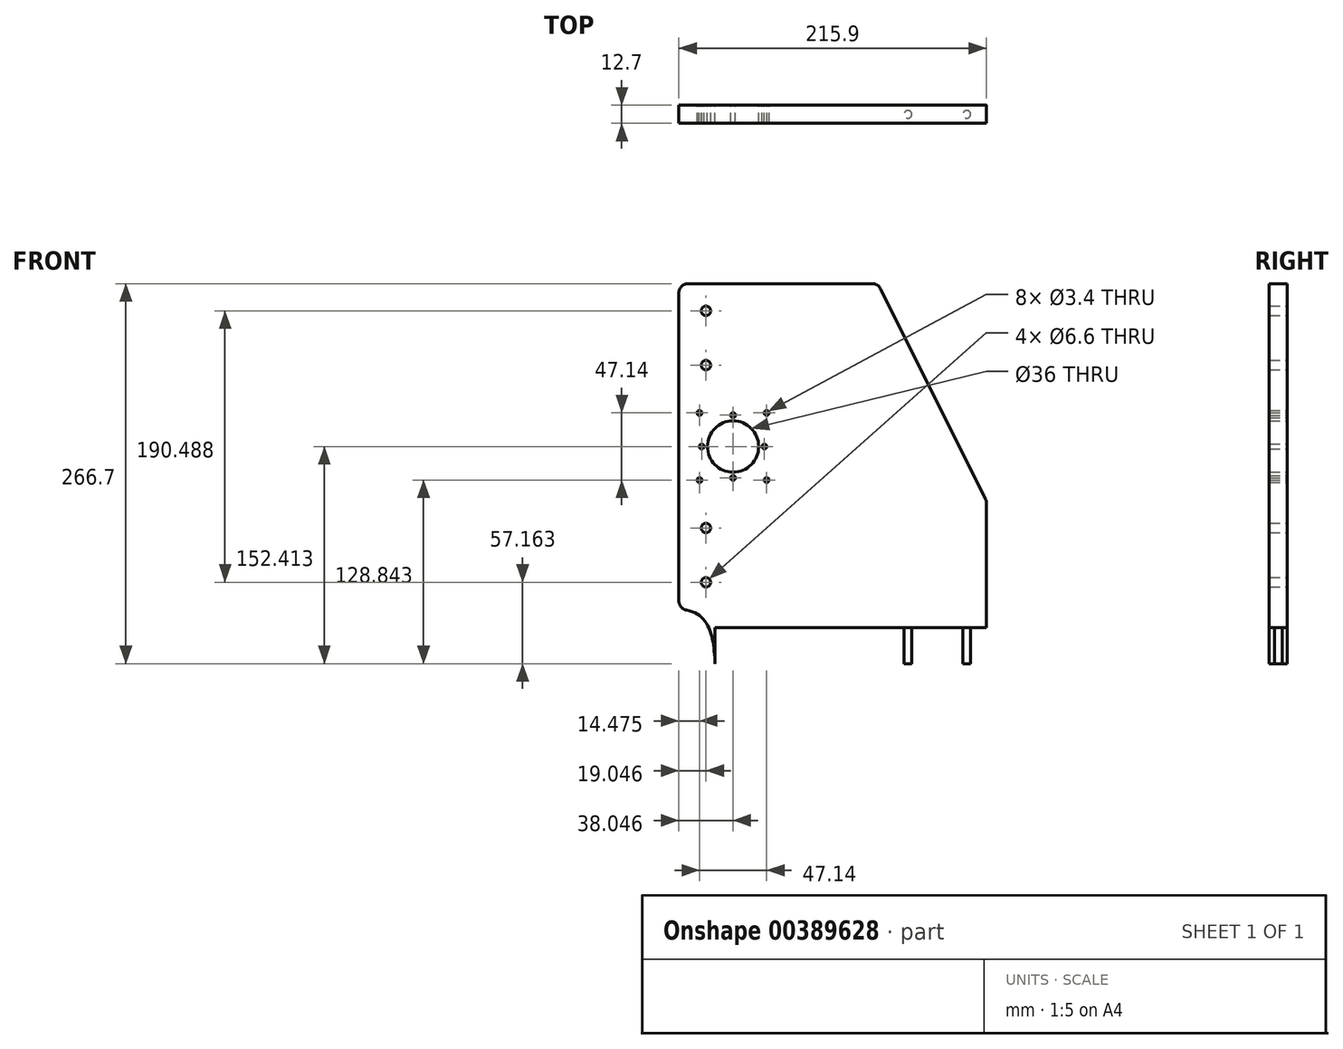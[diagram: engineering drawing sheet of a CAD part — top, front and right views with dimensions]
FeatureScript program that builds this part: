
annotation { "Feature Type Name" : "Feature", "Feature Type Description" : "" }
export const myFeature = defineFeature(function(context is Context, id is Id, definition is map)
    precondition{}
    {
        {
            var Q0;
            Q0=qCreatedBy(makeId("Front.planeOp"),FACE);
            var sketch = newSketch(context, id + "F0", { "sketchPlane" : qUnion([Q0])});
            skLineSegment(sketch, "E0.bottom", {"start": v(108.43, 152.4) * mm, "end": v(-107.47, 152.4) * mm});
            skLineSegment(sketch, "E0.left", {"start": v(108.43, 152.4) * mm, "end": v(108.43, -114.3) * mm});
            skLineSegment(sketch, "E0.right", {"start": v(-107.47, 152.4) * mm, "end": v(-107.47, -114.3) * mm});
            skPoint(sketch, "E0.middle", {"position": v(0, 0) * mm});
            skFitSpline(sketch, "E1", {"points": [v(-82.07, -114.3) * mm, v(-107.47, -76.2) * mm], "startDerivative": vector(-2.44, 55.55) * mm, "endDerivative": vector(-66.16, -0.04) * mm});
            skCircle(sketch, "E2", {"center": v(-88.42, -57.14) * mm, "radius": 3.3 * mm});
            skCircle(sketch, "E3", {"center": v(-88.42, -19.04) * mm, "radius": 3.3 * mm});
            skCircle(sketch, "E4", {"center": v(-88.42, 95.25) * mm, "radius": 3.3 * mm});
            skCircle(sketch, "E5", {"center": v(-88.42, 133.35) * mm, "radius": 3.3 * mm});
            skLineSegment(sketch, "E6", {"start": v(32.23, 152.4) * mm, "end": v(108.43, 0) * mm});
            skLineSegment(sketch, "E7", {"start": v(-107.47, -114.3) * mm, "end": v(108.43, -114.3) * mm});
            skLineSegment(sketch, "E8", {"start": v(-107.47, -76.2) * mm, "end": v(108.43, -76.2) * mm, "construction": true});
            skPoint(sketch, "E9.middle", {"position": v(-69.42, 38.11) * mm});
            skLineSegment(sketch, "E10", {"start": v(-69.42, 74.31) * mm, "end": v(-69.42, 11.11) * mm, "construction": true});
            skPoint(sketch, "E11.startSnap0", {"position": v(0.48, 152.4) * mm});
            skCircle(sketch, "E12", {"center": v(-69.42, 38.11) * mm, "radius": 18 * mm});
            skLineSegment(sketch, "E13", {"start": v(-98.77, 38.11) * mm, "end": v(-40.23, 38.11) * mm, "construction": true});
            skLineSegment(sketch, "E14", {"start": v(-91.1, 59.79) * mm, "end": v(-42.84, 11.53) * mm, "construction": true});
            skLineSegment(sketch, "E15", {"start": v(-49.22, 58.32) * mm, "end": v(-94.15, 13.39) * mm, "construction": true});
            skCircle(sketch, "E16", {"center": v(-93, 61.68) * mm, "radius": 1.7 * mm});
            skCircle(sketch, "E17.MirrorC", {"center": v(-93, 14.54) * mm, "radius": 1.7 * mm});
            skCircle(sketch, "E18.MirrorC", {"center": v(-45.85, 61.68) * mm, "radius": 1.7 * mm});
            skCircle(sketch, "E19.MirrorC", {"center": v(-45.85, 14.54) * mm, "radius": 1.7 * mm});
            skCircle(sketch, "E20", {"center": v(-69.42, 60.11) * mm, "radius": 1.7 * mm});
            skCircle(sketch, "E21.MirrorC", {"center": v(-69.42, 16.11) * mm, "radius": 1.7 * mm});
            skCircle(sketch, "E22", {"center": v(-91.42, 38.11) * mm, "radius": 1.7 * mm});
            skCircle(sketch, "E23.MirrorC", {"center": v(-47.42, 38.11) * mm, "radius": 1.7 * mm});
            skSolve(sketch);
        }
        {
            var Q0;
            {var subQ4=sQuery(id+"F0.wireOp",EDGE,"E1");Q0=makeQuery(id+"F0.imprint","IMPRINT",FACE,{"disambiguationData":[TD([[makeQuery(id+"F0.imprint","IMPRINT",EDGE,{"derivedFrom":subQ4}),-1.0]])]});}
            var Q1;
            Q1=makeQuery(id+"F0.imprint","IMPRINT",FACE,{"disambiguationData":[TD([[makeQuery(id+"F0.imprint","IMPRINT",EDGE,{"derivedFrom":sQuery(id+"F0.wireOp",EDGE,"d9uKs3Fb-to5y-7iI0-MEgy-WaLWoKfOPdlC")}),-1.0]])]});
            extrude(context, id + "F1", {"entities" : qUnion([Q0, Q1]), "depth" : 12.7 * mm});
        }
        {
            var Q0;
            {var subQ3=sQuery(id+"F0.wireOp",EDGE,"E1");Q0=makeQuery(id+"F0.imprint","IMPRINT",FACE,{"disambiguationData":[TD([[makeQuery(id+"F0.imprint","IMPRINT",EDGE,{"derivedFrom":subQ3}),1.0]])]});}
            var Q1;
            {var subQ2=sQuery(id+"F0.wireOp",EDGE,"E1");Q1=makeQuery(id+"F0.imprint","IMPRINT",FACE,{"disambiguationData":[TD([[makeQuery(id+"F0.imprint","IMPRINT",EDGE,{"derivedFrom":subQ2}),-1.0]])]});}
            extrude(context, id + "F2", {"entities" : qUnion([Q0, Q1]), "operationType" : NewBodyOperationType.REMOVE, "oppositeDirection" : true, "depth" : 25.4 * mm});
        }
        {
            var Q0;
            Q0=makeQuery(id+"F1.opExtrude","SWEPT_EDGE",EDGE,{"disambiguationData":[OSD([sQuery(id+"F0.wireOp",EDGE,"E0.right"),sQuery(id+"F0.wireOp",EDGE,"E1")])]});
            var Q1;
            Q1=makeQuery(id+"F1.opExtrude","SWEPT_EDGE",EDGE,{"disambiguationData":[OSD([sQuery(id+"F0.wireOp",EDGE,"E0.bottom"),sQuery(id+"F0.wireOp",EDGE,"E0.right")])]});
            var Q2;
            Q2=makeQuery(id+"F1.opExtrude","SWEPT_EDGE",EDGE,{"disambiguationData":[OSD([sQuery(id+"F0.wireOp",EDGE,"E0.bottom"),sQuery(id+"F0.wireOp",EDGE,"E11")])]});
            var Q3;
            Q3=makeQuery(id+"F1.opExtrude","SWEPT_EDGE",EDGE,{"disambiguationData":[OSD([sQuery(id+"F0.wireOp",EDGE,"E0.left"),sQuery(id+"F0.wireOp",EDGE,"E6")])]});
            fillet(context, id + "F3", {"entities" : qUnion([Q0, Q1, Q2, Q3]), "radius" : 6.35 * mm, "tangentPropagation" : true, "allowEdgeOverflow" : false});
        }
        {
            var Q0;
            Q0=makeQuery(id+"F1.opExtrude","SWEPT_FACE",FACE,{"disambiguationData":[OSD([sQuery(id+"F0.wireOp",EDGE,"E7")])]});
            var sketch = newSketch(context, id + "F4", { "sketchPlane" : qUnion([Q0])});
            skPoint(sketch, "E24.endSnap0", {"position": v(12.1, 6.35) * mm});
            skCircle(sketch, "E25", {"center": v(-70.45, 6.35) * mm, "radius": 2.7 * mm});
            skCircle(sketch, "E26", {"center": v(-29.17, 6.35) * mm, "radius": 2.7 * mm});
            skCircle(sketch, "E27", {"center": v(12.1, 6.35) * mm, "radius": 2.7 * mm});
            skCircle(sketch, "E28.MirrorC", {"center": v(94.65, 6.35) * mm, "radius": 2.7 * mm});
            skCircle(sketch, "E29.MirrorC", {"center": v(53.38, 6.35) * mm, "radius": 2.7 * mm});
            skSolve(sketch);
        }
        {
            var Q0;
            Q0=makeQuery(id+"F4.imprint","IMPRINT",FACE,{"disambiguationData":[TD([[makeQuery(id+"F4.imprint","IMPRINT",EDGE,{"derivedFrom":sQuery(id+"F4.wireOp",EDGE,"E25")}),1.0]])]});
            var Q1;
            Q1=makeQuery(id+"F4.imprint","IMPRINT",FACE,{"disambiguationData":[TD([[makeQuery(id+"F4.imprint","IMPRINT",EDGE,{"derivedFrom":sQuery(id+"F4.wireOp",EDGE,"E26")}),1.0]])]});
            var Q2;
            Q2=makeQuery(id+"F4.imprint","IMPRINT",FACE,{"disambiguationData":[TD([[makeQuery(id+"F4.imprint","IMPRINT",EDGE,{"derivedFrom":sQuery(id+"F4.wireOp",EDGE,"E27")}),1.0]])]});
            var Q3;
            Q3=makeQuery(id+"F4.imprint","IMPRINT",FACE,{"disambiguationData":[TD([[makeQuery(id+"F4.imprint","IMPRINT",EDGE,{"derivedFrom":sQuery(id+"F4.wireOp",EDGE,"E29.MirrorC")}),-1.0]])]});
            var Q4;
            Q4=makeQuery(id+"F4.imprint","IMPRINT",FACE,{"disambiguationData":[TD([[makeQuery(id+"F4.imprint","IMPRINT",EDGE,{"derivedFrom":sQuery(id+"F4.wireOp",EDGE,"E28.MirrorC")}),-1.0]])]});
            extrude(context, id + "F5", {"entities" : qUnion([Q0, Q1, Q2, Q3, Q4]), "operationType" : NewBodyOperationType.REMOVE, "oppositeDirection" : true, "depth" : 25.4 * mm, "offsetDistance" : 25.4 * mm});
        }
    });
